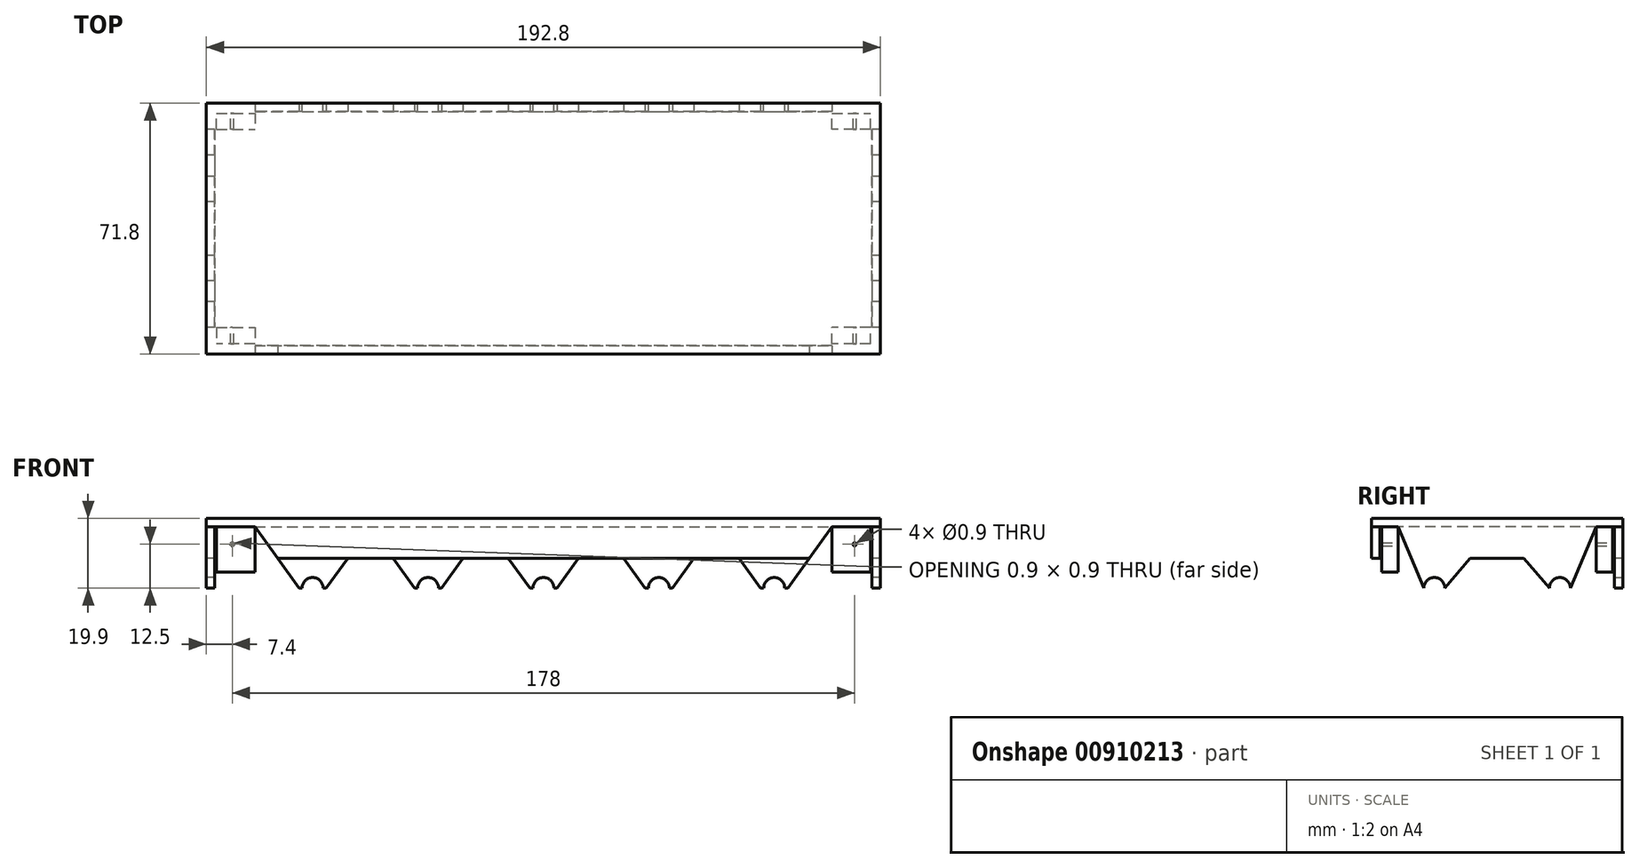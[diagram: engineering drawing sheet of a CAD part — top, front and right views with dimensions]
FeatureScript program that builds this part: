
annotation { "Feature Type Name" : "Feature", "Feature Type Description" : "" }
export const myFeature = defineFeature(function(context is Context, id is Id, definition is map)
    precondition{}
    {
        {
            var Q0;
            Q0=qCreatedBy(makeId("Top.planeOp"),FACE);
            var sketch = newSketch(context, id + "F0", { "sketchPlane" : qUnion([Q0])});
            skLineSegment(sketch, "E0.bottom", {"start": v(-94, 33.5) * mm, "end": v(94, 33.5) * mm});
            skLineSegment(sketch, "E0.top", {"start": v(-94, -33.5) * mm, "end": v(94, -33.5) * mm});
            skLineSegment(sketch, "E0.left", {"start": v(-94, 33.5) * mm, "end": v(-94, -33.5) * mm});
            skLineSegment(sketch, "E0.right", {"start": v(94, 33.5) * mm, "end": v(94, -33.5) * mm});
            skPoint(sketch, "E0.middle", {"position": v(0, 0) * mm});
            skLineSegment(sketch, "E1.bottom", {"start": v(-96.4, 35.9) * mm, "end": v(96.4, 35.9) * mm});
            skLineSegment(sketch, "E1.top", {"start": v(-96.4, -35.9) * mm, "end": v(96.4, -35.9) * mm});
            skLineSegment(sketch, "E1.left", {"start": v(-96.4, 35.9) * mm, "end": v(-96.4, -35.9) * mm});
            skLineSegment(sketch, "E1.right", {"start": v(96.4, 35.9) * mm, "end": v(96.4, -35.9) * mm});
            skSolve(sketch);
        }
        {
            var Q0;
            Q0=makeQuery(id+"F0.imprint","IMPRINT",FACE,{"disambiguationData":[TD([[makeQuery(id+"F0.imprint","IMPRINT",EDGE,{"derivedFrom":sQuery(id+"F0.wireOp",EDGE,"E0.bottom")}),1.0]])]});
            extrude(context, id + "F1", {"entities" : qUnion([Q0]), "depth" : 35 * mm, "offsetDistance" : 25 * mm});
        }
        {
            var Q0;
            Q0=makeQuery(id+"F1.opExtrude","SWEPT_FACE",FACE,{"disambiguationData":[OSD([sQuery(id+"F0.wireOp",EDGE,"E1.left")])]});
            var sketch = newSketch(context, id + "F2", { "sketchPlane" : qUnion([Q0])});
            skLineSegment(sketch, "E2", {"start": v(-35.9, 17.5) * mm, "end": v(35.9, 17.5) * mm, "construction": true});
            skPoint(sketch, "E3", {"position": v(0, 17.5) * mm});
            skLineSegment(sketch, "E4", {"start": v(-35.9, 17.5) * mm, "end": v(0, 17.5) * mm, "construction": true});
            skLineSegment(sketch, "E5", {"start": v(0, 17.5) * mm, "end": v(35.9, 17.5) * mm, "construction": true});
            skPoint(sketch, "E6", {"position": v(-17.95, 17.5) * mm});
            skPoint(sketch, "E7", {"position": v(17.95, 17.5) * mm});
            skCircle(sketch, "E8", {"center": v(-17.95, 17.5) * mm, "radius": 3 * mm});
            skCircle(sketch, "E9", {"center": v(17.95, 17.5) * mm, "radius": 3 * mm});
            skSolve(sketch);
        }
        {
            var Q0;
            Q0=makeQuery(id+"F2.imprint","IMPRINT",FACE,{"disambiguationData":[TD([[makeQuery(id+"F2.imprint","IMPRINT",EDGE,{"derivedFrom":sQuery(id+"F2.wireOp",EDGE,"E8")}),1.0]])]});
            var Q1;
            Q1=makeQuery(id+"F2.imprint","IMPRINT",FACE,{"disambiguationData":[TD([[makeQuery(id+"F2.imprint","IMPRINT",EDGE,{"derivedFrom":sQuery(id+"F2.wireOp",EDGE,"E9")}),1.0]])]});
            extrude(context, id + "F3", {"entities" : qUnion([Q0, Q1]), "operationType" : NewBodyOperationType.REMOVE, "endBound" : BoundingType.THROUGH_ALL, "oppositeDirection" : true, "depth" : 25 * mm, "offsetDistance" : 25 * mm});
        }
        {
            var Q0;
            Q0=makeQuery(id+"F1.opExtrude","SWEPT_FACE",FACE,{"disambiguationData":[OSD([sQuery(id+"F0.wireOp",EDGE,"E1.top")])]});
            var sketch = newSketch(context, id + "F4", { "sketchPlane" : qUnion([Q0])});
            skLineSegment(sketch, "E10", {"start": v(0, 35) * mm, "end": v(0, 0) * mm, "construction": true});
            skPoint(sketch, "E11", {"position": v(0, 17.5) * mm});
            skCircle(sketch, "E12", {"center": v(0, 17.5) * mm, "radius": 3.9 * mm});
            skCircle(sketch, "E13.1.0.0", {"center": v(33, 17.5) * mm, "radius": 3.9 * mm});
            skCircle(sketch, "E13.2.0.0", {"center": v(66, 17.5) * mm, "radius": 3.9 * mm});
            skLineSegment(sketch, "E13.direction1", {"start": v(0, 17.5) * mm, "end": v(33, 17.5) * mm, "construction": true});
            skCircle(sketch, "E14.1.0.0", {"center": v(-33, 17.5) * mm, "radius": 3.9 * mm});
            skCircle(sketch, "E14.2.0.0", {"center": v(-66, 17.5) * mm, "radius": 3.9 * mm});
            skLineSegment(sketch, "E14.direction1", {"start": v(0, 17.5) * mm, "end": v(-33, 17.5) * mm, "construction": true});
            skSolve(sketch);
        }
        {
            var Q0;
            Q0=qSketchRegion(id+"F4",true);
            extrude(context, id + "F5", {"entities" : qUnion([Q0]), "operationType" : NewBodyOperationType.REMOVE, "oppositeDirection" : true, "depth" : 25 * mm, "offsetDistance" : 25 * mm});
        }
        {
            var Q0;
            Q0=makeQuery(id+"F1.opExtrude","SWEPT_FACE",FACE,{"disambiguationData":[OSD([sQuery(id+"F0.wireOp",EDGE,"E1.bottom")])]});
            var sketch = newSketch(context, id + "F6", { "sketchPlane" : qUnion([Q0])});
            skLineSegment(sketch, "E15", {"start": v(0, 35) * mm, "end": v(0, 0) * mm, "construction": true});
            skLineSegment(sketch, "E16", {"start": v(-96.4, 17.5) * mm, "end": v(96.4, 17.5) * mm, "construction": true});
            skPoint(sketch, "E17", {"position": v(0, 17.5) * mm});
            skCircle(sketch, "E18", {"center": v(0, 17.5) * mm, "radius": 3 * mm});
            skCircle(sketch, "E19.1.0.0", {"center": v(33, 17.5) * mm, "radius": 3 * mm});
            skCircle(sketch, "E19.2.0.0", {"center": v(66, 17.5) * mm, "radius": 3 * mm});
            skLineSegment(sketch, "E19.direction1", {"start": v(0, 17.5) * mm, "end": v(33, 17.5) * mm, "construction": true});
            skCircle(sketch, "E20.1.0.0", {"center": v(-33, 17.5) * mm, "radius": 3 * mm});
            skCircle(sketch, "E20.2.0.0", {"center": v(-66, 17.5) * mm, "radius": 3 * mm});
            skLineSegment(sketch, "E20.direction1", {"start": v(0, 17.5) * mm, "end": v(-33, 17.5) * mm, "construction": true});
            skSolve(sketch);
        }
        {
            var Q0;
            Q0=qSketchRegion(id+"F6",true);
            extrude(context, id + "F7", {"entities" : qUnion([Q0]), "operationType" : NewBodyOperationType.REMOVE, "oppositeDirection" : true, "depth" : 25 * mm, "offsetDistance" : 25 * mm});
        }
        {
            var Q0;
            Q0=makeQuery(id+"F1.opExtrude","CAP_FACE",FACE,{"disambiguationData":[OSD([sQuery(id+"F0.wireOp",EDGE,"E0.bottom"),sQuery(id+"F0.wireOp",EDGE,"E0.top"),sQuery(id+"F0.wireOp",EDGE,"E0.left"),sQuery(id+"F0.wireOp",EDGE,"E0.right"),sQuery(id+"F0.wireOp",EDGE,"E1.bottom"),sQuery(id+"F0.wireOp",EDGE,"E1.top"),sQuery(id+"F0.wireOp",EDGE,"E1.left"),sQuery(id+"F0.wireOp",EDGE,"E1.right")])],"isStart":false});
            var sketch = newSketch(context, id + "F8", { "sketchPlane" : qUnion([Q0])});
            skLineSegment(sketch, "E21", {"start": v(96.4, 0) * mm, "end": v(-96.4, 0) * mm, "construction": true});
            skLineSegment(sketch, "E22", {"start": v(0, -33.5) * mm, "end": v(0, 33.5) * mm, "construction": true});
            skLineSegment(sketch, "E23", {"start": v(96.4, -35.9) * mm, "end": v(96.4, 0) * mm, "construction": true});
            skLineSegment(sketch, "E24", {"start": v(96.4, 35.9) * mm, "end": v(96.4, 0) * mm, "construction": true});
            skLineSegment(sketch, "E25", {"start": v(-96.4, -35.9) * mm, "end": v(-96.4, 0) * mm, "construction": true});
            skLineSegment(sketch, "E26", {"start": v(-96.4, 35.9) * mm, "end": v(-96.4, 0) * mm, "construction": true});
            skPoint(sketch, "E27", {"position": v(96.4, -17.95) * mm});
            skPoint(sketch, "E28", {"position": v(96.4, 17.95) * mm});
            skPoint(sketch, "E29", {"position": v(-96.4, -17.95) * mm});
            skPoint(sketch, "E30", {"position": v(-96.4, 17.95) * mm});
            skCircle(sketch, "E31", {"center": v(-96.4, 35.9) * mm, "radius": 7.5 * mm, "construction": true});
            skCircle(sketch, "E32", {"center": v(-96.4, -35.9) * mm, "radius": 7.5 * mm, "construction": true});
            skCircle(sketch, "E33", {"center": v(96.4, 35.9) * mm, "radius": 7.5 * mm, "construction": true});
            skCircle(sketch, "E34", {"center": v(96.4, -35.9) * mm, "radius": 7.5 * mm, "construction": true});
            skPoint(sketch, "E35", {"position": v(-96.4, 28.4) * mm});
            skPoint(sketch, "E36", {"position": v(-96.4, -28.4) * mm});
            skPoint(sketch, "E37", {"position": v(96.4, 28.4) * mm});
            skPoint(sketch, "E38", {"position": v(96.4, -28.4) * mm});
            skPoint(sketch, "E39", {"position": v(0, 35.9) * mm});
            skPoint(sketch, "E40", {"position": v(0, -35.9) * mm});
            skPoint(sketch, "E41.1.0.0", {"position": v(33, 35.9) * mm});
            skPoint(sketch, "E41.2.0.0", {"position": v(66, 35.9) * mm});
            skLineSegment(sketch, "E41.direction1", {"start": v(0, 35.9) * mm, "end": v(33, 35.9) * mm, "construction": true});
            skPoint(sketch, "E42.1.0.0", {"position": v(-33, 35.9) * mm});
            skPoint(sketch, "E42.2.0.0", {"position": v(-66, 35.9) * mm});
            skLineSegment(sketch, "E42.direction1", {"start": v(0, 35.9) * mm, "end": v(-33, 35.9) * mm, "construction": true});
            skPoint(sketch, "E43.1.0.0", {"position": v(33, -35.9) * mm});
            skPoint(sketch, "E43.2.0.0", {"position": v(66, -35.9) * mm});
            skLineSegment(sketch, "E43.direction1", {"start": v(0, -35.9) * mm, "end": v(33, -35.9) * mm, "construction": true});
            skPoint(sketch, "E44.1.0.0", {"position": v(-33, -35.9) * mm});
            skPoint(sketch, "E44.2.0.0", {"position": v(-66, -35.9) * mm});
            skLineSegment(sketch, "E44.direction1", {"start": v(0, -35.9) * mm, "end": v(-33, -35.9) * mm, "construction": true});
            skSolve(sketch);
        }
        {
            var Q0;
            Q0=makeQuery(id+"F1.opExtrude","SWEPT_FACE",FACE,{"disambiguationData":[OSD([sQuery(id+"F0.wireOp",EDGE,"E1.left")])]});
            var sketch = newSketch(context, id + "F9", { "sketchPlane" : qUnion([Q0])});
            skPoint(sketch, "E45", {"position": v(-20.95, 17.5) * mm});
            skPoint(sketch, "E45.positionSnap0", {"position": v(-35.9, 17.5) * mm});
            skPoint(sketch, "E46", {"position": v(20.95, 17.5) * mm});
            skPoint(sketch, "E46.positionSnap0", {"position": v(35.9, 17.5) * mm});
            skPoint(sketch, "E47", {"position": v(14.95, 17.5) * mm});
            skPoint(sketch, "E48", {"position": v(-14.95, 17.5) * mm});
            skLineSegment(sketch, "E49", {"start": v(-28.37, 35) * mm, "end": v(-20.95, 17.5) * mm});
            skLineSegment(sketch, "E50", {"start": v(-14.95, 17.5) * mm, "end": v(0, 35) * mm});
            skLineSegment(sketch, "E51", {"start": v(0, 35) * mm, "end": v(14.95, 17.5) * mm});
            skLineSegment(sketch, "E52", {"start": v(20.95, 17.5) * mm, "end": v(28.32, 35) * mm});
            skLineSegment(sketch, "E53", {"start": v(-35.9, 26) * mm, "end": v(35.9, 26) * mm});
            skSolve(sketch);
        }
        {
            var Q0;
            Q0=makeQuery(id+"F1.opExtrude","SWEPT_FACE",FACE,{"disambiguationData":[OSD([sQuery(id+"F0.wireOp",EDGE,"E1.top")])]});
            var sketch = newSketch(context, id + "F10", { "sketchPlane" : qUnion([Q0])});
            skPoint(sketch, "E54", {"position": v(-69.9, 17.5) * mm});
            skPoint(sketch, "E54.positionSnap0", {"position": v(-96.4, 17.5) * mm});
            skPoint(sketch, "E55", {"position": v(-62.1, 17.5) * mm});
            skPoint(sketch, "E56", {"position": v(-36.9, 17.5) * mm});
            skPoint(sketch, "E57", {"position": v(-29.1, 17.5) * mm});
            skPoint(sketch, "E58", {"position": v(-3.9, 17.5) * mm});
            skPoint(sketch, "E59", {"position": v(3.9, 17.5) * mm});
            skPoint(sketch, "E60", {"position": v(29.1, 17.5) * mm});
            skPoint(sketch, "E61", {"position": v(36.9, 17.5) * mm});
            skPoint(sketch, "E62", {"position": v(62.1, 17.5) * mm});
            skPoint(sketch, "E63", {"position": v(69.9, 17.5) * mm});
            skPoint(sketch, "E64", {"position": v(0, 35) * mm});
            skPoint(sketch, "E65.1.0.0", {"position": v(16.5, 35) * mm});
            skPoint(sketch, "E65.2.0.0", {"position": v(33, 35) * mm});
            skPoint(sketch, "E65.3.0.0", {"position": v(49.5, 35) * mm});
            skPoint(sketch, "E65.4.0.0", {"position": v(66, 35) * mm});
            skPoint(sketch, "E65.5.0.0", {"position": v(82.5, 35) * mm});
            skLineSegment(sketch, "E65.direction1", {"start": v(0, 35) * mm, "end": v(16.5, 35) * mm, "construction": true});
            skPoint(sketch, "E66.1.0.0", {"position": v(-16.5, 35) * mm});
            skPoint(sketch, "E66.2.0.0", {"position": v(-33, 35) * mm});
            skPoint(sketch, "E66.3.0.0", {"position": v(-49.5, 35) * mm});
            skPoint(sketch, "E66.4.0.0", {"position": v(-66, 35) * mm});
            skPoint(sketch, "E66.5.0.0", {"position": v(-82.5, 35) * mm});
            skLineSegment(sketch, "E66.direction1", {"start": v(0, 35) * mm, "end": v(-16.5, 35) * mm, "construction": true});
            skLineSegment(sketch, "E67", {"start": v(-82.5, 35) * mm, "end": v(-69.9, 17.5) * mm});
            skLineSegment(sketch, "E68", {"start": v(-69.9, 17.5) * mm, "end": v(-62.1, 17.5) * mm});
            skLineSegment(sketch, "E69", {"start": v(-62.1, 17.5) * mm, "end": v(-49.5, 35) * mm});
            skLineSegment(sketch, "E70", {"start": v(-49.5, 35) * mm, "end": v(-36.9, 17.5) * mm});
            skLineSegment(sketch, "E71", {"start": v(-36.9, 17.5) * mm, "end": v(-29.1, 17.5) * mm});
            skLineSegment(sketch, "E72", {"start": v(-29.1, 17.5) * mm, "end": v(-16.5, 35) * mm});
            skLineSegment(sketch, "E73", {"start": v(-16.5, 35) * mm, "end": v(-3.9, 17.5) * mm});
            skLineSegment(sketch, "E74", {"start": v(-3.9, 17.5) * mm, "end": v(3.9, 17.5) * mm});
            skLineSegment(sketch, "E75", {"start": v(3.9, 17.5) * mm, "end": v(16.5, 35) * mm});
            skLineSegment(sketch, "E76", {"start": v(16.5, 35) * mm, "end": v(29.1, 17.5) * mm});
            skLineSegment(sketch, "E77", {"start": v(29.1, 17.5) * mm, "end": v(36.9, 17.5) * mm});
            skLineSegment(sketch, "E78", {"start": v(36.9, 17.5) * mm, "end": v(49.5, 35) * mm});
            skLineSegment(sketch, "E79", {"start": v(49.5, 35) * mm, "end": v(62.1, 17.5) * mm});
            skLineSegment(sketch, "E80", {"start": v(62.1, 17.5) * mm, "end": v(69.9, 17.5) * mm});
            skLineSegment(sketch, "E81", {"start": v(69.9, 17.5) * mm, "end": v(82.5, 35) * mm});
            skLineSegment(sketch, "E82", {"start": v(-96.4, 26) * mm, "end": v(96.4, 26) * mm});
            skLineSegment(sketch, "E83", {"start": v(-94, 35) * mm, "end": v(-94, 0) * mm});
            skLineSegment(sketch, "E84", {"start": v(94, 35) * mm, "end": v(94, 0) * mm});
            skSolve(sketch);
        }
        {
            var Q0;
            Q0=makeQuery(id+"F8.imprint","IMPRINT",FACE,{"disambiguationData":[TD([[makeQuery(id+"F8.imprint","IMPRINT",EDGE,{"derivedFrom":makeQuery(id+"F1.opExtrude","CAP_EDGE",EDGE,{"disambiguationData":[OSD([sQuery(id+"F0.wireOp",EDGE,"E0.bottom")])],"isStart":false})}),1.0]])]});
            var Q1;
            Q1=makeQuery(id+"F8.imprint","IMPRINT",FACE,{"disambiguationData":[TD([[makeQuery(id+"F8.imprint","IMPRINT",EDGE,{"derivedFrom":makeQuery(id+"F1.opExtrude","CAP_EDGE",EDGE,{"disambiguationData":[OSD([sQuery(id+"F0.wireOp",EDGE,"E0.bottom")])],"isStart":false})}),-1.0]])]});
            extrude(context, id + "F11", {"entities" : qUnion([Q0, Q1]), "operationType" : NewBodyOperationType.ADD, "depth" : 2.4 * mm, "offsetDistance" : 25 * mm});
        }
        {
            var Q0;
            {var subQ10=sQuery(id+"F10.wireOp",EDGE,"E82");var subQ20=sQuery(id+"F10.wireOp",EDGE,"E67");var subQ23=makeQuery(id+"F10.imprint","INTERSECT",VERTEX,{"derivedFrom":[subQ20,subQ10]});Q0=makeQuery(id+"F10.imprint","IMPRINT",FACE,{"disambiguationData":[TD([[makeQuery(id+"F10.imprint","IMPRINT",EDGE,{"disambiguationData":[TD([[subQ23,1.0]])],"derivedFrom":subQ10}),-1.0]])]});}
            var Q1;
            {var subQ0=sQuery(id+"F10.wireOp",EDGE,"E67");var subQ1=makeQuery(id+"F1.opExtrude","CAP_EDGE",EDGE,{"disambiguationData":[OSD([sQuery(id+"F0.wireOp",EDGE,"E1.top")])],"isStart":false});var subQ2=makeQuery(id+"F10.imprint","INTERSECT",VERTEX,{"derivedFrom":[subQ1,subQ0]});Q1=makeQuery(id+"F10.imprint","IMPRINT",FACE,{"disambiguationData":[TD([[makeQuery(id+"F10.imprint","IMPRINT",EDGE,{"disambiguationData":[TD([[subQ2,-1.0]])],"derivedFrom":subQ0}),-1.0]])]});}
            var Q2;
            {var subQ0=sQuery(id+"F10.wireOp",EDGE,"E81");var subQ1=makeQuery(id+"F1.opExtrude","CAP_EDGE",EDGE,{"disambiguationData":[OSD([sQuery(id+"F0.wireOp",EDGE,"E1.top")])],"isStart":false});var subQ2=makeQuery(id+"F10.imprint","INTERSECT",VERTEX,{"derivedFrom":[subQ1,subQ0]});Q2=makeQuery(id+"F10.imprint","IMPRINT",FACE,{"disambiguationData":[TD([[makeQuery(id+"F10.imprint","IMPRINT",EDGE,{"disambiguationData":[TD([[subQ2,1.0]])],"derivedFrom":subQ0}),-1.0]])]});}
            var Q3;
            {var subQ0=sQuery(id+"F10.wireOp",EDGE,"E68");Q3=makeQuery(id+"F10.imprint","IMPRINT",FACE,{"disambiguationData":[TD([[makeQuery(id+"F10.imprint","IMPRINT",EDGE,{"derivedFrom":subQ0}),-1.0]])]});}
            var Q4;
            {var subQ0=sQuery(id+"F10.wireOp",EDGE,"E71");Q4=makeQuery(id+"F10.imprint","IMPRINT",FACE,{"disambiguationData":[TD([[makeQuery(id+"F10.imprint","IMPRINT",EDGE,{"derivedFrom":subQ0}),-1.0]])]});}
            var Q5;
            {var subQ0=sQuery(id+"F10.wireOp",EDGE,"E74");Q5=makeQuery(id+"F10.imprint","IMPRINT",FACE,{"disambiguationData":[TD([[makeQuery(id+"F10.imprint","IMPRINT",EDGE,{"derivedFrom":subQ0}),-1.0]])]});}
            var Q6;
            {var subQ0=sQuery(id+"F10.wireOp",EDGE,"E77");Q6=makeQuery(id+"F10.imprint","IMPRINT",FACE,{"disambiguationData":[TD([[makeQuery(id+"F10.imprint","IMPRINT",EDGE,{"derivedFrom":subQ0}),-1.0]])]});}
            var Q7;
            {var subQ0=sQuery(id+"F10.wireOp",EDGE,"E80");Q7=makeQuery(id+"F10.imprint","IMPRINT",FACE,{"disambiguationData":[TD([[makeQuery(id+"F10.imprint","IMPRINT",EDGE,{"derivedFrom":subQ0}),-1.0]])]});}
            extrude(context, id + "F12", {"entities" : qUnion([Q0, Q1, Q2, Q3, Q4, Q5, Q6, Q7]), "operationType" : NewBodyOperationType.REMOVE, "endBound" : BoundingType.THROUGH_ALL, "oppositeDirection" : true, "depth" : 25 * mm, "offsetDistance" : 25 * mm});
        }
        {
            var Q0;
            {var subQ0=sQuery(id+"F0.wireOp",EDGE,"E1.left");var subQ1=makeQuery(id+"F1.opExtrude","CAP_EDGE",EDGE,{"disambiguationData":[OSD([subQ0])],"isStart":true});Q0=makeQuery(id+"F9.imprint","IMPRINT",FACE,{"disambiguationData":[TD([[makeQuery(id+"F9.imprint","IMPRINT",EDGE,{"derivedFrom":subQ1}),1.0]])]});}
            var Q1;
            {var subQ0=sQuery(id+"F9.wireOp",EDGE,"E49");var subQ1=sQuery(id+"F0.wireOp",EDGE,"E1.left");var subQ2=makeQuery(id+"F1.opExtrude","CAP_EDGE",EDGE,{"disambiguationData":[OSD([subQ1])],"isStart":false});var subQ3=makeQuery(id+"F9.imprint","INTERSECT",VERTEX,{"derivedFrom":[subQ2,subQ0]});Q1=makeQuery(id+"F9.imprint","IMPRINT",FACE,{"disambiguationData":[TD([[makeQuery(id+"F9.imprint","IMPRINT",EDGE,{"disambiguationData":[TD([[subQ3,-1.0]])],"derivedFrom":subQ0}),-1.0]])]});}
            var Q2;
            {var subQ0=sQuery(id+"F9.wireOp",EDGE,"E52");var subQ1=sQuery(id+"F0.wireOp",EDGE,"E1.left");var subQ2=makeQuery(id+"F1.opExtrude","CAP_EDGE",EDGE,{"disambiguationData":[OSD([subQ1])],"isStart":false});var subQ3=makeQuery(id+"F9.imprint","INTERSECT",VERTEX,{"derivedFrom":[subQ2,subQ0]});Q2=makeQuery(id+"F9.imprint","IMPRINT",FACE,{"disambiguationData":[TD([[makeQuery(id+"F9.imprint","IMPRINT",EDGE,{"disambiguationData":[TD([[subQ3,1.0]])],"derivedFrom":subQ0}),-1.0]])]});}
            extrude(context, id + "F13", {"entities" : qUnion([Q0, Q1, Q2]), "operationType" : NewBodyOperationType.REMOVE, "oppositeDirection" : true, "depth" : 5 * mm, "offsetDistance" : 25 * mm});
        }
        {
            var Q0;
            {var subQ0=sQuery(id+"F9.wireOp",EDGE,"E49");var subQ1=sQuery(id+"F0.wireOp",EDGE,"E1.left");var subQ2=makeQuery(id+"F1.opExtrude","CAP_EDGE",EDGE,{"disambiguationData":[OSD([subQ1])],"isStart":false});var subQ3=makeQuery(id+"F9.imprint","INTERSECT",VERTEX,{"derivedFrom":[subQ2,subQ0]});Q0=makeQuery(id+"F9.imprint","IMPRINT",FACE,{"disambiguationData":[TD([[makeQuery(id+"F9.imprint","IMPRINT",EDGE,{"disambiguationData":[TD([[subQ3,-1.0]])],"derivedFrom":subQ0}),-1.0]])]});}
            var Q1;
            {var subQ0=sQuery(id+"F9.wireOp",EDGE,"E52");var subQ1=sQuery(id+"F0.wireOp",EDGE,"E1.left");var subQ2=makeQuery(id+"F1.opExtrude","CAP_EDGE",EDGE,{"disambiguationData":[OSD([subQ1])],"isStart":false});var subQ3=makeQuery(id+"F9.imprint","INTERSECT",VERTEX,{"derivedFrom":[subQ2,subQ0]});Q1=makeQuery(id+"F9.imprint","IMPRINT",FACE,{"disambiguationData":[TD([[makeQuery(id+"F9.imprint","IMPRINT",EDGE,{"disambiguationData":[TD([[subQ3,1.0]])],"derivedFrom":subQ0}),-1.0]])]});}
            var Q2;
            {var subQ0=sQuery(id+"F0.wireOp",EDGE,"E1.left");var subQ1=makeQuery(id+"F1.opExtrude","CAP_EDGE",EDGE,{"disambiguationData":[OSD([subQ0])],"isStart":true});Q2=makeQuery(id+"F9.imprint","IMPRINT",FACE,{"disambiguationData":[TD([[makeQuery(id+"F9.imprint","IMPRINT",EDGE,{"derivedFrom":subQ1}),1.0]])]});}
            extrude(context, id + "F14", {"entities" : qUnion([Q0, Q1, Q2]), "operationType" : NewBodyOperationType.REMOVE, "oppositeDirection" : true, "depth" : 204.7 * mm, "offsetDistance" : 25 * mm, "hasSecondDirection" : true, "secondDirectionOppositeDirection" : true, "secondDirectionDepth" : 183.4 * mm});
        }
        {
            var Q0;
            {var subQ0=sQuery(id+"F0.wireOp",EDGE,"E1.left");var subQ1=makeQuery(id+"F1.opExtrude","CAP_EDGE",EDGE,{"disambiguationData":[OSD([subQ0])],"isStart":false});var subQ2=sQuery(id+"F0.wireOp",EDGE,"E1.top");var subQ3=makeQuery(id+"F9.imprint","IMPRINT",EDGE,{"disambiguationData":[TD([[makeQuery(id+"F9.imprint","INTERSECT",VERTEX,{"derivedFrom":[subQ1,sQuery(id+"F9.wireOp",EDGE,"E52")]}),-1.0]])],"derivedFrom":subQ1});var subQ4=sQuery(id+"F0.wireOp",EDGE,"E1.bottom");var subQ5=makeQuery(id+"F9.imprint","IMPRINT",EDGE,{"disambiguationData":[TD([[makeQuery(id+"F9.imprint","INTERSECT",VERTEX,{"derivedFrom":[subQ1,sQuery(id+"F9.wireOp",EDGE,"E49")]}),1.0]])],"derivedFrom":subQ1});var subQ6=makeQuery(id+"F1.opExtrude","CAP_EDGE",EDGE,{"disambiguationData":[OSD([subQ2])],"isStart":false});Q0=makeQuery(id+"F14.boolean.opBoolean","MERGE",FACE,{"derivedFrom":[makeQuery(id+"F13.boolean.opBoolean","MERGE",FACE,{"derivedFrom":[makeQuery(id+"F12.boolean.opBoolean","MERGE",FACE,{"derivedFrom":[makeQuery(id+"F11.opExtrude","CAP_FACE",FACE,{"disambiguationData":[OSD([subQ4,subQ2,subQ0,sQuery(id+"F0.wireOp",EDGE,"E1.right")])],"isStart":true})],"fromTools":[makeQuery(id+"F12.opExtrude","SWEPT_FACE",FACE,{"disambiguationData":[OSD([subQ2]),TDD([makeQuery(id+"F10.imprint","IMPRINT",EDGE,{"disambiguationData":[TD([[makeQuery(id+"F10.imprint","INTERSECT",VERTEX,{"derivedFrom":[subQ6,sQuery(id+"F10.wireOp",EDGE,"E67")]}),1.0]])],"derivedFrom":subQ6})])]}),makeQuery(id+"F12.opExtrude","SWEPT_FACE",FACE,{"disambiguationData":[OSD([subQ2]),TDD([makeQuery(id+"F10.imprint","IMPRINT",EDGE,{"disambiguationData":[TD([[makeQuery(id+"F10.imprint","INTERSECT",VERTEX,{"derivedFrom":[subQ6,sQuery(id+"F10.wireOp",EDGE,"E81")]}),-1.0]])],"derivedFrom":subQ6})])]})]})],"fromTools":[makeQuery(id+"F13.opExtrude","SWEPT_FACE",FACE,{"disambiguationData":[OSD([subQ0]),TDD([subQ5])]}),makeQuery(id+"F13.opExtrude","SWEPT_FACE",FACE,{"disambiguationData":[OSD([subQ0]),TDD([subQ3])]})]})],"fromTools":[makeQuery(id+"F14.opExtrude","SWEPT_FACE",FACE,{"disambiguationData":[OSD([subQ0]),TDD([subQ5])]}),makeQuery(id+"F14.opExtrude","SWEPT_FACE",FACE,{"disambiguationData":[OSD([subQ0]),TDD([subQ3])]})]});}
            var sketch = newSketch(context, id + "F15", { "sketchPlane" : qUnion([Q0])});
            skLineSegment(sketch, "E85", {"start": v(-94, 33.5) * mm, "end": v(-94, 28.32) * mm});
            skLineSegment(sketch, "E86", {"start": v(-94, 28.32) * mm, "end": v(-82.5, 28.32) * mm});
            skLineSegment(sketch, "E87", {"start": v(-82.5, 28.32) * mm, "end": v(-82.5, 33.5) * mm});
            skLineSegment(sketch, "E88", {"start": v(-82.5, 33.5) * mm, "end": v(-94, 33.5) * mm});
            skLineSegment(sketch, "E89.bottom", {"start": v(-94, -33.5) * mm, "end": v(-82.5, -33.5) * mm});
            skLineSegment(sketch, "E89.top", {"start": v(-94, -28.37) * mm, "end": v(-82.5, -28.37) * mm});
            skLineSegment(sketch, "E89.left", {"start": v(-94, -33.5) * mm, "end": v(-94, -28.37) * mm});
            skLineSegment(sketch, "E89.right", {"start": v(-82.5, -33.5) * mm, "end": v(-82.5, -28.37) * mm});
            skLineSegment(sketch, "E90.bottom", {"start": v(94, 33.5) * mm, "end": v(82.5, 33.5) * mm});
            skLineSegment(sketch, "E90.top", {"start": v(94, 28.32) * mm, "end": v(82.5, 28.32) * mm});
            skLineSegment(sketch, "E90.left", {"start": v(94, 33.5) * mm, "end": v(94, 28.32) * mm});
            skLineSegment(sketch, "E90.right", {"start": v(82.5, 33.5) * mm, "end": v(82.5, 28.32) * mm});
            skLineSegment(sketch, "E91.bottom", {"start": v(94, -28.37) * mm, "end": v(82.5, -28.37) * mm});
            skLineSegment(sketch, "E91.top", {"start": v(94, -33.5) * mm, "end": v(82.5, -33.5) * mm});
            skLineSegment(sketch, "E91.left", {"start": v(94, -28.37) * mm, "end": v(94, -33.5) * mm});
            skLineSegment(sketch, "E91.right", {"start": v(82.5, -28.37) * mm, "end": v(82.5, -33.5) * mm});
            skLineSegment(sketch, "E92.bottom", {"start": v(-82.5, 28.32) * mm, "end": v(-93.5, 28.32) * mm});
            skLineSegment(sketch, "E92.top", {"start": v(-82.5, 33) * mm, "end": v(-93.5, 33) * mm});
            skLineSegment(sketch, "E92.left", {"start": v(-82.5, 28.32) * mm, "end": v(-82.5, 33) * mm});
            skLineSegment(sketch, "E92.right", {"start": v(-93.5, 28.32) * mm, "end": v(-93.5, 33) * mm});
            skLineSegment(sketch, "E93.bottom", {"start": v(-93.5, -28.37) * mm, "end": v(-82.5, -28.37) * mm});
            skLineSegment(sketch, "E93.top", {"start": v(-93.5, -33) * mm, "end": v(-82.5, -33) * mm});
            skLineSegment(sketch, "E93.left", {"start": v(-93.5, -28.37) * mm, "end": v(-93.5, -33) * mm});
            skLineSegment(sketch, "E93.right", {"start": v(-82.5, -28.37) * mm, "end": v(-82.5, -33) * mm});
            skLineSegment(sketch, "E94.bottom", {"start": v(82.5, -28.37) * mm, "end": v(93.5, -28.37) * mm});
            skLineSegment(sketch, "E94.top", {"start": v(82.5, -33) * mm, "end": v(93.5, -33) * mm});
            skLineSegment(sketch, "E94.left", {"start": v(82.5, -28.37) * mm, "end": v(82.5, -33) * mm});
            skLineSegment(sketch, "E94.right", {"start": v(93.5, -28.37) * mm, "end": v(93.5, -33) * mm});
            skLineSegment(sketch, "E95.bottom", {"start": v(93.5, 33) * mm, "end": v(82.5, 33) * mm});
            skLineSegment(sketch, "E95.top", {"start": v(93.5, 28.32) * mm, "end": v(82.5, 28.32) * mm});
            skLineSegment(sketch, "E95.left", {"start": v(93.5, 33) * mm, "end": v(93.5, 28.32) * mm});
            skLineSegment(sketch, "E95.right", {"start": v(82.5, 33) * mm, "end": v(82.5, 28.32) * mm});
            skLineSegment(sketch, "E96.bottom", {"start": v(-93.5, 28.32) * mm, "end": v(-82.5, 28.32) * mm});
            skLineSegment(sketch, "E96.top", {"start": v(-93.5, 25) * mm, "end": v(-82.5, 25) * mm});
            skLineSegment(sketch, "E96.left", {"start": v(-93.5, 28.32) * mm, "end": v(-93.5, 25) * mm});
            skLineSegment(sketch, "E96.right", {"start": v(-82.5, 28.32) * mm, "end": v(-82.5, 25) * mm});
            skLineSegment(sketch, "E97.bottom", {"start": v(-82.5, -28.37) * mm, "end": v(-93.5, -28.37) * mm});
            skLineSegment(sketch, "E97.top", {"start": v(-82.5, -25) * mm, "end": v(-93.5, -25) * mm});
            skLineSegment(sketch, "E97.left", {"start": v(-82.5, -28.37) * mm, "end": v(-82.5, -25) * mm});
            skLineSegment(sketch, "E97.right", {"start": v(-93.5, -28.37) * mm, "end": v(-93.5, -25) * mm});
            skLineSegment(sketch, "E98.bottom", {"start": v(93.5, -28.37) * mm, "end": v(82.5, -28.37) * mm});
            skLineSegment(sketch, "E98.top", {"start": v(93.5, -28.37) * mm, "end": v(82.5, -28.37) * mm});
            skLineSegment(sketch, "E98.left", {"start": v(93.5, -28.37) * mm, "end": v(93.5, -28.37) * mm});
            skLineSegment(sketch, "E98.right", {"start": v(82.5, -28.37) * mm, "end": v(82.5, -28.37) * mm});
            skLineSegment(sketch, "E99.top", {"start": v(93.5, -25) * mm, "end": v(82.5, -25) * mm});
            skLineSegment(sketch, "E99.left", {"start": v(93.5, -28.37) * mm, "end": v(93.5, -25) * mm});
            skLineSegment(sketch, "E99.right", {"start": v(82.5, -28.37) * mm, "end": v(82.5, -25) * mm});
            skLineSegment(sketch, "E100.bottom", {"start": v(82.5, 28.32) * mm, "end": v(93.5, 28.32) * mm});
            skLineSegment(sketch, "E100.top", {"start": v(82.5, 25) * mm, "end": v(93.5, 25) * mm});
            skLineSegment(sketch, "E100.left", {"start": v(82.5, 28.32) * mm, "end": v(82.5, 25) * mm});
            skLineSegment(sketch, "E100.right", {"start": v(93.5, 28.32) * mm, "end": v(93.5, 25) * mm});
            skSolve(sketch);
        }
        {
            var Q0;
            Q0=makeQuery(id+"F15.imprint","IMPRINT",FACE,{"disambiguationData":[TD([[makeQuery(id+"F15.imprint","IMPRINT",EDGE,{"derivedFrom":sQuery(id+"F15.wireOp",EDGE,"E92.bottom")}),-1.0]])]});
            var Q1;
            Q1=makeQuery(id+"F15.imprint","IMPRINT",FACE,{"disambiguationData":[TD([[makeQuery(id+"F15.imprint","IMPRINT",EDGE,{"derivedFrom":sQuery(id+"F15.wireOp",EDGE,"E93.bottom")}),-1.0]])]});
            var Q2;
            Q2=makeQuery(id+"F15.imprint","IMPRINT",FACE,{"disambiguationData":[TD([[makeQuery(id+"F15.imprint","IMPRINT",EDGE,{"derivedFrom":sQuery(id+"F15.wireOp",EDGE,"E94.bottom")}),-1.0]])]});
            var Q3;
            Q3=makeQuery(id+"F15.imprint","IMPRINT",FACE,{"disambiguationData":[TD([[makeQuery(id+"F15.imprint","IMPRINT",EDGE,{"derivedFrom":sQuery(id+"F15.wireOp",EDGE,"E95.bottom")}),1.0]])]});
            var Q4;
            Q4=makeQuery(id+"F15.imprint","IMPRINT",FACE,{"disambiguationData":[TD([[makeQuery(id+"F15.imprint","IMPRINT",EDGE,{"derivedFrom":sQuery(id+"F15.wireOp",EDGE,"E100.bottom")}),-1.0]])]});
            var Q5;
            Q5=makeQuery(id+"F15.imprint","IMPRINT",FACE,{"disambiguationData":[TD([[makeQuery(id+"F15.imprint","IMPRINT",EDGE,{"derivedFrom":sQuery(id+"F15.wireOp",EDGE,"E94.top")}),1.0]])]});
            var Q6;
            Q6=makeQuery(id+"F15.imprint","IMPRINT",FACE,{"disambiguationData":[TD([[makeQuery(id+"F15.imprint","IMPRINT",EDGE,{"derivedFrom":sQuery(id+"F15.wireOp",EDGE,"E98.bottom")}),-1.0]])]});
            var Q7;
            Q7=makeQuery(id+"F15.imprint","IMPRINT",FACE,{"disambiguationData":[TD([[makeQuery(id+"F15.imprint","IMPRINT",EDGE,{"derivedFrom":sQuery(id+"F15.wireOp",EDGE,"E93.top")}),1.0]])]});
            var Q8;
            Q8=makeQuery(id+"F15.imprint","IMPRINT",FACE,{"disambiguationData":[TD([[makeQuery(id+"F15.imprint","IMPRINT",EDGE,{"derivedFrom":sQuery(id+"F15.wireOp",EDGE,"E97.bottom")}),-1.0]])]});
            var Q9;
            Q9=makeQuery(id+"F15.imprint","IMPRINT",FACE,{"disambiguationData":[TD([[makeQuery(id+"F15.imprint","IMPRINT",EDGE,{"derivedFrom":sQuery(id+"F15.wireOp",EDGE,"E96.bottom")}),-1.0]])]});
            var Q10;
            Q10=makeQuery(id+"F15.imprint","IMPRINT",FACE,{"disambiguationData":[TD([[makeQuery(id+"F15.imprint","IMPRINT",EDGE,{"derivedFrom":sQuery(id+"F15.wireOp",EDGE,"E92.top")}),1.0]])]});
            extrude(context, id + "F16", {"entities" : qUnion([Q0, Q1, Q2, Q3, Q4, Q5, Q6, Q7, Q8, Q9, Q10]), "operationType" : NewBodyOperationType.ADD, "depth" : 13 * mm, "offsetDistance" : 25 * mm});
        }
        {
            var Q0;
            {var subQ1=sQuery(id+"F10.wireOp",EDGE,"E67");var subQ4=sQuery(id+"F10.wireOp",EDGE,"E82");var subQ5=makeQuery(id+"F10.imprint","INTERSECT",VERTEX,{"derivedFrom":[subQ1,subQ4]});Q0=makeQuery(id+"F10.imprint","IMPRINT",FACE,{"disambiguationData":[TD([[makeQuery(id+"F10.imprint","IMPRINT",EDGE,{"disambiguationData":[TD([[subQ5,-1.0]])],"derivedFrom":subQ4}),-1.0]])]});}
            var Q1;
            {var subQ1=sQuery(id+"F10.wireOp",EDGE,"E70");var subQ4=sQuery(id+"F10.wireOp",EDGE,"E82");var subQ5=makeQuery(id+"F10.imprint","INTERSECT",VERTEX,{"derivedFrom":[subQ1,subQ4]});Q1=makeQuery(id+"F10.imprint","IMPRINT",FACE,{"disambiguationData":[TD([[makeQuery(id+"F10.imprint","IMPRINT",EDGE,{"disambiguationData":[TD([[subQ5,-1.0]])],"derivedFrom":subQ4}),-1.0]])]});}
            var Q2;
            {var subQ1=sQuery(id+"F10.wireOp",EDGE,"E73");var subQ4=sQuery(id+"F10.wireOp",EDGE,"E82");var subQ5=makeQuery(id+"F10.imprint","INTERSECT",VERTEX,{"derivedFrom":[subQ1,subQ4]});Q2=makeQuery(id+"F10.imprint","IMPRINT",FACE,{"disambiguationData":[TD([[makeQuery(id+"F10.imprint","IMPRINT",EDGE,{"disambiguationData":[TD([[subQ5,-1.0]])],"derivedFrom":subQ4}),-1.0]])]});}
            var Q3;
            {var subQ1=sQuery(id+"F10.wireOp",EDGE,"E76");var subQ4=sQuery(id+"F10.wireOp",EDGE,"E82");var subQ5=makeQuery(id+"F10.imprint","INTERSECT",VERTEX,{"derivedFrom":[subQ1,subQ4]});Q3=makeQuery(id+"F10.imprint","IMPRINT",FACE,{"disambiguationData":[TD([[makeQuery(id+"F10.imprint","IMPRINT",EDGE,{"disambiguationData":[TD([[subQ5,-1.0]])],"derivedFrom":subQ4}),-1.0]])]});}
            var Q4;
            {var subQ1=sQuery(id+"F10.wireOp",EDGE,"E79");var subQ4=sQuery(id+"F10.wireOp",EDGE,"E82");var subQ5=makeQuery(id+"F10.imprint","INTERSECT",VERTEX,{"derivedFrom":[subQ1,subQ4]});Q4=makeQuery(id+"F10.imprint","IMPRINT",FACE,{"disambiguationData":[TD([[makeQuery(id+"F10.imprint","IMPRINT",EDGE,{"disambiguationData":[TD([[subQ5,-1.0]])],"derivedFrom":subQ4}),-1.0]])]});}
            extrude(context, id + "F17", {"entities" : qUnion([Q0, Q1, Q2, Q3, Q4]), "operationType" : NewBodyOperationType.REMOVE, "oppositeDirection" : true, "depth" : 25 * mm, "offsetDistance" : 25 * mm});
        }
        {
            var Q0;
            Q0=makeQuery(id+"F16.opExtrude","SWEPT_FACE",FACE,{"disambiguationData":[OSD([sQuery(id+"F15.wireOp",EDGE,"E94.top")])]});
            var sketch = newSketch(context, id + "F18", { "sketchPlane" : qUnion([Q0])});
            skCircle(sketch, "E101", {"center": v(-89, 30) * mm, "radius": 0.45 * mm});
            skCircle(sketch, "E102", {"center": v(89, 30) * mm, "radius": 0.45 * mm});
            skSolve(sketch);
        }
        {
            var Q0;
            Q0 = qSketchRegion(id + "F18", true);
            extrude(context, id + "F19", {"entities" : qUnion([Q0]), "operationType" : NewBodyOperationType.REMOVE, "endBound" : BoundingType.THROUGH_ALL, "oppositeDirection" : true, "depth" : 25 * mm, "offsetDistance" : 25 * mm});
        }
    });
